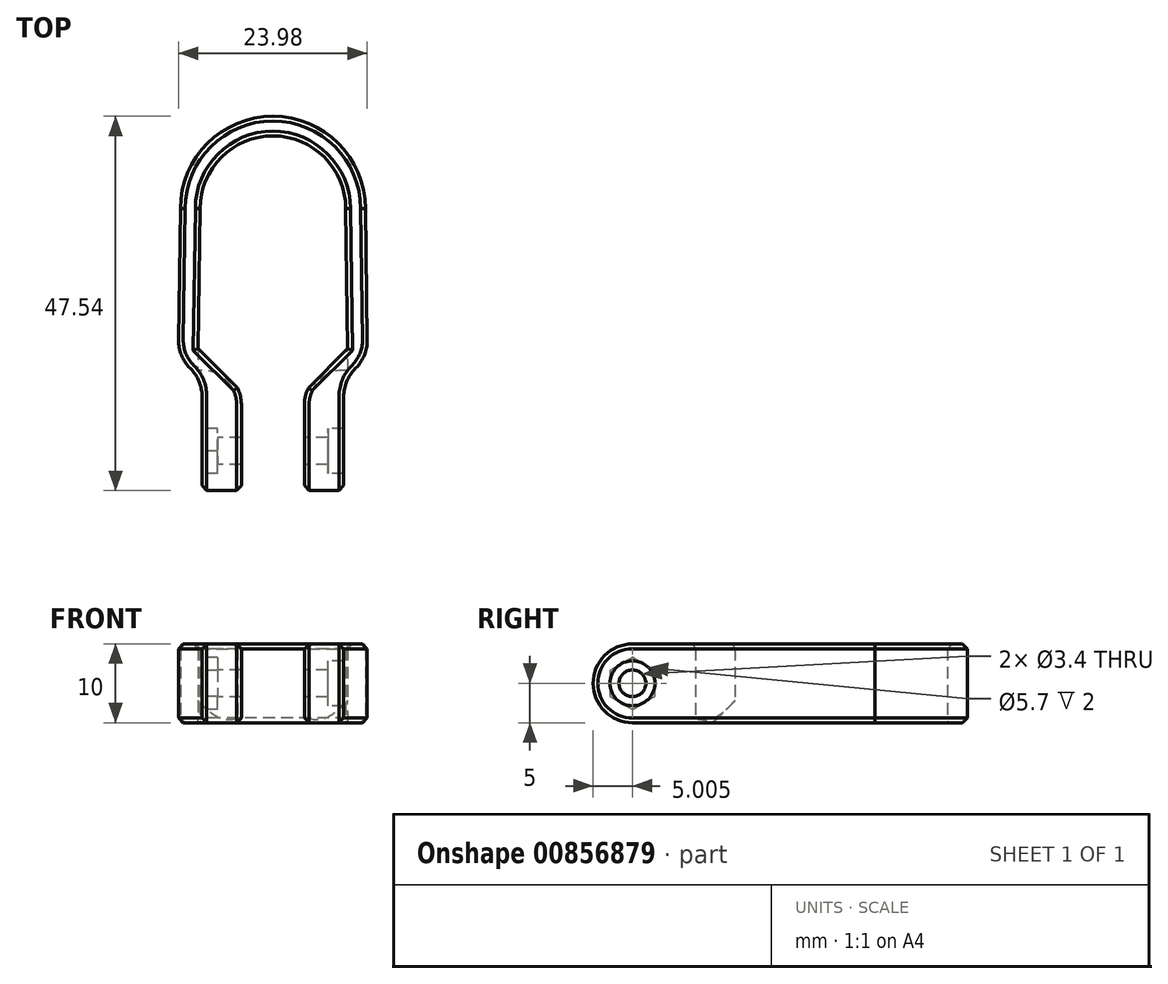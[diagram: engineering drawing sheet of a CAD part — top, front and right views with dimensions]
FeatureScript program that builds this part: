
annotation { "Feature Type Name" : "Feature", "Feature Type Description" : "" }
export const myFeature = defineFeature(function(context is Context, id is Id, definition is map)
    precondition{}
    {
        {
            var Q0;
            Q0=qCreatedBy(makeId("Top.planeOp"),FACE);
            var sketch = newSketch(context, id + "F0", { "sketchPlane" : qUnion([Q0])});
            skArc(sketch, "E0", {"start": v(9.25, 0) * mm, "mid": v(0, 9.25) * mm, "end": v(-9.25, 0) * mm});
            skLineSegment(sketch, "E1", {"start": v(-4.5, -22.75) * mm, "end": v(4.5, -22.75) * mm});
            skPoint(sketch, "E2", {"position": v(0, -22.75) * mm});
            skLineSegment(sketch, "E3", {"start": v(-9.5, -17.75) * mm, "end": v(-9.25, 0) * mm});
            skLineSegment(sketch, "E4", {"start": v(9.25, 0) * mm, "end": v(9.5, -17.75) * mm});
            skLineSegment(sketch, "E5", {"start": v(-9.5, -17.75) * mm, "end": v(-4.5, -22.75) * mm});
            skLineSegment(sketch, "E6.MirrorCS", {"start": v(9.5, -17.75) * mm, "end": v(4.5, -22.75) * mm});
            skPoint(sketch, "E7.orphan", {"position": v(-9.57, -22.75) * mm});
            skPoint(sketch, "E8.orphan", {"position": v(9.57, -22.75) * mm});
            skLineSegment(sketch, "E9.0", {"start": v(11.75, 0.02) * mm, "end": v(12.01, -18.77) * mm});
            skLineSegment(sketch, "E9.1", {"start": v(-4, -25.25) * mm, "end": v(5.54, -25.25) * mm});
            skLineSegment(sketch, "E9.2", {"start": v(-12.01, -18.77) * mm, "end": v(-5.54, -25.25) * mm});
            skLineSegment(sketch, "E9.3", {"start": v(12.01, -18.77) * mm, "end": v(5.54, -25.25) * mm});
            skLineSegment(sketch, "E9.4", {"start": v(-12.01, -18.77) * mm, "end": v(-11.75, 0.02) * mm});
            skArc(sketch, "E9.5", {"start": v(11.75, 0.02) * mm, "mid": v(0, 11.75) * mm, "end": v(-11.75, 0.02) * mm});
            skLineSegment(sketch, "E10", {"start": v(-4, -22.75) * mm, "end": v(-4, -25.25) * mm});
            skLineSegment(sketch, "E11.MirrorCS", {"start": v(4, -22.75) * mm, "end": v(4, -25.25) * mm});
            skLineSegment(sketch, "E12.bottom", {"start": v(-5.54, -25.25) * mm, "end": v(-3, -25.25) * mm});
            skLineSegment(sketch, "E13.bottom", {"start": v(-9, -21.79) * mm, "end": v(-4, -21.79) * mm});
            skLineSegment(sketch, "E13.top", {"start": v(-9, -35.79) * mm, "end": v(-4, -35.79) * mm});
            skLineSegment(sketch, "E13.left", {"start": v(-9, -21.79) * mm, "end": v(-9, -35.79) * mm});
            skLineSegment(sketch, "E13.right", {"start": v(-4, -21.79) * mm, "end": v(-4, -35.79) * mm});
            skLineSegment(sketch, "E14.MirrorCS", {"start": v(4, -21.79) * mm, "end": v(4, -35.79) * mm});
            skLineSegment(sketch, "E15.MirrorCS", {"start": v(9, -35.79) * mm, "end": v(4, -35.79) * mm});
            skLineSegment(sketch, "E16.MirrorCS", {"start": v(9, -21.79) * mm, "end": v(9, -35.79) * mm});
            skLineSegment(sketch, "E17.MirrorCS", {"start": v(9, -21.79) * mm, "end": v(4, -21.79) * mm});
            skSolve(sketch);
        }
        {
            var Q0;
            Q0=makeQuery(id+"F0.imprint","IMPRINT",FACE,{"disambiguationData":[TD([[makeQuery(id+"F0.imprint","IMPRINT",EDGE,{"derivedFrom":sQuery(id+"F0.wireOp",EDGE,"E0")}),-1.0]])]});
            var Q1;
            Q1=makeQuery(id+"F0.imprint","IMPRINT",FACE,{"disambiguationData":[TD([[makeQuery(id+"F0.imprint","IMPRINT",EDGE,{"derivedFrom":sQuery(id+"F0.wireOp",EDGE,"E12.bottom")}),-1.0]])]});
            var Q2;
            {var subQ0=sQuery(id+"F0.wireOp",EDGE,"b47a069d-5063-4df7-93ab-cb99865989350.MirrorCS");Q2=makeQuery(id+"F0.imprint","IMPRINT",FACE,{"disambiguationData":[TD([[makeQuery(id+"F0.imprint","IMPRINT",EDGE,{"derivedFrom":subQ0}),-1.0]])]});}
            var Q3;
            {var subQ0=sQuery(id+"F0.wireOp",EDGE,"E15.MirrorCS");Q3=makeQuery(id+"F0.imprint","IMPRINT",FACE,{"disambiguationData":[TD([[makeQuery(id+"F0.imprint","IMPRINT",EDGE,{"derivedFrom":subQ0}),-1.0]])]});}
            var Q4;
            {var subQ7=sQuery(id+"F0.wireOp",EDGE,"E5");var subQ8=sQuery(id+"F0.wireOp",EDGE,"E1");var subQ9=makeQuery(id+"F0.imprint","INTERSECT",VERTEX,{"derivedFrom":[subQ8,subQ7]});Q4=makeQuery(id+"F0.imprint","IMPRINT",FACE,{"disambiguationData":[TD([[makeQuery(id+"F0.imprint","IMPRINT",EDGE,{"disambiguationData":[TD([[subQ9,-1.0]])],"derivedFrom":subQ8}),-1.0]])]});}
            var Q5;
            {var subQ7=sQuery(id+"F0.wireOp",EDGE,"E6.MirrorCS");var subQ8=sQuery(id+"F0.wireOp",EDGE,"E1");var subQ9=makeQuery(id+"F0.imprint","INTERSECT",VERTEX,{"derivedFrom":[subQ8,subQ7]});Q5=makeQuery(id+"F0.imprint","IMPRINT",FACE,{"disambiguationData":[TD([[makeQuery(id+"F0.imprint","IMPRINT",EDGE,{"disambiguationData":[TD([[subQ9,1.0]])],"derivedFrom":subQ8}),-1.0]])]});}
            extrude(context, id + "F1", {"entities" : qUnion([Q0, Q1, Q2, Q3, Q4, Q5]), "depth" : 10 * mm, "offsetDistance" : 25 * mm});
        }
        {
            var Q0;
            Q0=makeQuery(id+"F1.opExtrude","CAP_EDGE",EDGE,{"disambiguationData":[OSD([sQuery(id+"F0.wireOp",EDGE,"E12.top")])],"isStart":false});
            var Q1;
            Q1=makeQuery(id+"F1.opExtrude","CAP_EDGE",EDGE,{"disambiguationData":[OSD([sQuery(id+"F0.wireOp",EDGE,"62c8df0b-8da3-4cad-a578-fa849236712b0.MirrorCS")])],"isStart":false});
            var Q2;
            Q2=makeQuery(id+"F1.opExtrude","CAP_EDGE",EDGE,{"disambiguationData":[OSD([sQuery(id+"F0.wireOp",EDGE,"62c8df0b-8da3-4cad-a578-fa849236712b0.MirrorCS")])],"isStart":true});
            var Q3;
            Q3=makeQuery(id+"F1.opExtrude","CAP_EDGE",EDGE,{"disambiguationData":[OSD([sQuery(id+"F0.wireOp",EDGE,"E12.top")])],"isStart":true});
            var Q4;
            Q4=makeQuery(id+"F1.opExtrude","CAP_EDGE",EDGE,{"disambiguationData":[OSD([sQuery(id+"F0.wireOp",EDGE,"E13.top")])],"isStart":false});
            var Q5;
            Q5=makeQuery(id+"F1.opExtrude","CAP_EDGE",EDGE,{"disambiguationData":[OSD([sQuery(id+"F0.wireOp",EDGE,"E13.top")])],"isStart":true});
            var Q6;
            Q6=makeQuery(id+"F1.opExtrude","CAP_EDGE",EDGE,{"disambiguationData":[OSD([sQuery(id+"F0.wireOp",EDGE,"E15.MirrorCS")])],"isStart":false});
            var Q7;
            Q7=makeQuery(id+"F1.opExtrude","CAP_EDGE",EDGE,{"disambiguationData":[OSD([sQuery(id+"F0.wireOp",EDGE,"E15.MirrorCS")])],"isStart":true});
            fillet(context, id + "F2", {"entities" : qUnion([Q0, Q1, Q2, Q3, Q4, Q5, Q6, Q7]), "radius" : 5 * mm, "tangentPropagation" : true, "allowEdgeOverflow" : false});
        }
        {
            var Q0;
            Q0=makeQuery(id+"F1.opExtrude","SWEPT_FACE",FACE,{"disambiguationData":[OSD([sQuery(id+"F0.wireOp",EDGE,"E13.left")])]});
            var sketch = newSketch(context, id + "F3", { "sketchPlane" : qUnion([Q0])});
            skCircle(sketch, "E18", {"center": v(30.79, 5) * mm, "radius": 1.7 * mm});
            skPoint(sketch, "E18.centerSnap0", {"position": v(35.79, 5) * mm});
            skCircle(sketch, "E19.cCircle", {"center": v(30.79, 5) * mm, "radius": 2.85 * mm});
            skLineSegment(sketch, "E19.0", {"start": v(27.94, 3.35) * mm, "end": v(27.94, 6.65) * mm});
            skLineSegment(sketch, "E19.1", {"start": v(27.94, 6.65) * mm, "end": v(30.79, 8.3) * mm});
            skLineSegment(sketch, "E19.2", {"start": v(30.79, 8.3) * mm, "end": v(33.64, 6.65) * mm});
            skLineSegment(sketch, "E19.3", {"start": v(33.64, 6.65) * mm, "end": v(33.64, 3.35) * mm});
            skLineSegment(sketch, "E19.4", {"start": v(33.64, 3.35) * mm, "end": v(30.79, 1.7) * mm});
            skLineSegment(sketch, "E19.5", {"start": v(30.79, 1.7) * mm, "end": v(27.94, 3.35) * mm});
            skPoint(sketch, "E19.0.midPoint", {"position": v(27.94, 5) * mm});
            skSolve(sketch);
        }
        {
            var Q0;
            Q0=makeQuery(id+"F3.imprint","IMPRINT",FACE,{"disambiguationData":[TD([[makeQuery(id+"F3.imprint","IMPRINT",EDGE,{"derivedFrom":sQuery(id+"F3.wireOp",EDGE,"E18")}),1.0]])]});
            extrude(context, id + "F4", {"entities" : qUnion([Q0]), "operationType" : NewBodyOperationType.REMOVE, "endBound" : BoundingType.THROUGH_ALL, "oppositeDirection" : true, "depth" : 25 * mm, "offsetDistance" : 25 * mm});
        }
        {
            var Q0;
            Q0=makeQuery(id+"F3.imprint","IMPRINT",FACE,{"disambiguationData":[TD([[makeQuery(id+"F3.imprint","IMPRINT",EDGE,{"derivedFrom":sQuery(id+"F3.wireOp",EDGE,"E18")}),-1.0]])]});
            var Q1;
            {var subQ0=sQuery(id+"F3.wireOp",EDGE,"E19.0");var subQ1=sQuery(id+"F3.wireOp",EDGE,"E19.cCircle");var subQ2=makeQuery(id+"F3.imprint","INTERSECT",VERTEX,{"derivedFrom":[subQ1,subQ0]});Q1=makeQuery(id+"F3.imprint","IMPRINT",FACE,{"disambiguationData":[TD([[makeQuery(id+"F3.imprint","IMPRINT",EDGE,{"disambiguationData":[TD([[subQ2,-1.0]])],"derivedFrom":subQ1}),-1.0]])]});}
            var Q2;
            {var subQ0=sQuery(id+"F3.wireOp",EDGE,"E19.1");var subQ1=sQuery(id+"F3.wireOp",EDGE,"E19.cCircle");var subQ2=makeQuery(id+"F3.imprint","INTERSECT",VERTEX,{"derivedFrom":[subQ1,subQ0]});Q2=makeQuery(id+"F3.imprint","IMPRINT",FACE,{"disambiguationData":[TD([[makeQuery(id+"F3.imprint","IMPRINT",EDGE,{"disambiguationData":[TD([[subQ2,-1.0]])],"derivedFrom":subQ1}),-1.0]])]});}
            var Q3;
            {var subQ0=sQuery(id+"F3.wireOp",EDGE,"E19.2");var subQ1=sQuery(id+"F3.wireOp",EDGE,"E19.cCircle");var subQ2=makeQuery(id+"F3.imprint","INTERSECT",VERTEX,{"derivedFrom":[subQ1,subQ0]});Q3=makeQuery(id+"F3.imprint","IMPRINT",FACE,{"disambiguationData":[TD([[makeQuery(id+"F3.imprint","IMPRINT",EDGE,{"disambiguationData":[TD([[subQ2,-1.0]])],"derivedFrom":subQ1}),-1.0]])]});}
            var Q4;
            {var subQ0=sQuery(id+"F3.wireOp",EDGE,"E19.2");var subQ1=sQuery(id+"F3.wireOp",EDGE,"E19.cCircle");var subQ2=makeQuery(id+"F3.imprint","INTERSECT",VERTEX,{"derivedFrom":[subQ1,subQ0]});Q4=makeQuery(id+"F3.imprint","IMPRINT",FACE,{"disambiguationData":[TD([[makeQuery(id+"F3.imprint","IMPRINT",EDGE,{"disambiguationData":[TD([[subQ2,1.0]])],"derivedFrom":subQ1}),-1.0]])]});}
            var Q5;
            {var subQ0=sQuery(id+"F3.wireOp",EDGE,"E19.3");var subQ1=sQuery(id+"F3.wireOp",EDGE,"E19.cCircle");var subQ2=makeQuery(id+"F3.imprint","INTERSECT",VERTEX,{"derivedFrom":[subQ1,subQ0]});Q5=makeQuery(id+"F3.imprint","IMPRINT",FACE,{"disambiguationData":[TD([[makeQuery(id+"F3.imprint","IMPRINT",EDGE,{"disambiguationData":[TD([[subQ2,1.0]])],"derivedFrom":subQ1}),-1.0]])]});}
            var Q6;
            {var subQ0=sQuery(id+"F3.wireOp",EDGE,"E19.5");var subQ1=sQuery(id+"F3.wireOp",EDGE,"E19.cCircle");var subQ2=makeQuery(id+"F3.imprint","INTERSECT",VERTEX,{"derivedFrom":[subQ1,subQ0]});Q6=makeQuery(id+"F3.imprint","IMPRINT",FACE,{"disambiguationData":[TD([[makeQuery(id+"F3.imprint","IMPRINT",EDGE,{"disambiguationData":[TD([[subQ2,-1.0]])],"derivedFrom":subQ1}),-1.0]])]});}
            extrude(context, id + "F5", {"entities" : qUnion([Q0, Q1, Q2, Q3, Q4, Q5, Q6]), "operationType" : NewBodyOperationType.REMOVE, "oppositeDirection" : true, "depth" : 2 * mm, "offsetDistance" : 25 * mm});
        }
        {
            var Q0;
            Q0=makeQuery(id+"F3.imprint","IMPRINT",FACE,{"disambiguationData":[TD([[makeQuery(id+"F3.imprint","IMPRINT",EDGE,{"derivedFrom":sQuery(id+"F3.wireOp",EDGE,"E18")}),-1.0]])]});
            var Q1;
            Q1=makeQuery(id+"F1.opExtrude","SWEPT_FACE",FACE,{"disambiguationData":[OSD([sQuery(id+"F0.wireOp",EDGE,"E16.MirrorCS")])]});
            var Q2;
            Q2=makeQuery(id+"F1.opExtrude","SWEPT_FACE",FACE,{"disambiguationData":[OSD([sQuery(id+"F0.wireOp",EDGE,"E14.MirrorCS")])]});
            extrude(context, id + "F6", {"entities" : qUnion([Q0]), "operationType" : NewBodyOperationType.REMOVE, "endBound" : BoundingType.UP_TO_SURFACE, "oppositeDirection" : true, "depth" : 25 * mm, "endBoundEntityFace" : qUnion([Q1]), "offsetDistance" : 25 * mm, "hasSecondDirection" : true, "secondDirectionBound" : SecondDirectionBoundingType.UP_TO_SURFACE, "secondDirectionOppositeDirection" : true, "secondDirectionDepth" : 9.7 * mm, "secondDirectionBoundEntityFace" : qUnion([Q2]), "hasSecondDirectionOffset" : true, "secondDirectionOffsetDistance" : -3 * mm});
        }
        {
            var Q0;
            Q0=makeQuery(id+"F1.opExtrude","SWEPT_EDGE",EDGE,{"disambiguationData":[OSD([sQuery(id+"F0.wireOp",EDGE,"E9.2"),sQuery(id+"F0.wireOp",EDGE,"E13.bottom"),sQuery(id+"F0.wireOp",EDGE,"E13.left")])]});
            var Q1;
            Q1=makeQuery(id+"F1.opExtrude","SWEPT_EDGE",EDGE,{"disambiguationData":[OSD([sQuery(id+"F0.wireOp",EDGE,"E9.3"),sQuery(id+"F0.wireOp",EDGE,"E16.MirrorCS"),sQuery(id+"F0.wireOp",EDGE,"E17.MirrorCS")])]});
            var Q2;
            Q2=makeQuery(id+"F1.opExtrude","SWEPT_EDGE",EDGE,{"disambiguationData":[OSD([sQuery(id+"F0.wireOp",EDGE,"E9.0"),sQuery(id+"F0.wireOp",EDGE,"E9.3")])]});
            var Q3;
            Q3=makeQuery(id+"F1.opExtrude","SWEPT_EDGE",EDGE,{"disambiguationData":[OSD([sQuery(id+"F0.wireOp",EDGE,"E9.2"),sQuery(id+"F0.wireOp",EDGE,"E9.4")])]});
            fillet(context, id + "F7", {"entities" : qUnion([Q0, Q1, Q2, Q3]), "radius" : 5 * mm, "tangentPropagation" : true, "allowEdgeOverflow" : false});
        }
        {
            var Q0;
            Q0=makeQuery(id+"F1.opExtrude","SWEPT_EDGE",EDGE,{"disambiguationData":[OSD([sQuery(id+"F0.wireOp",EDGE,"E1"),sQuery(id+"F0.wireOp",EDGE,"E13.right")])]});
            var Q1;
            Q1=makeQuery(id+"F1.opExtrude","SWEPT_EDGE",EDGE,{"disambiguationData":[OSD([sQuery(id+"F0.wireOp",EDGE,"E1"),sQuery(id+"F0.wireOp",EDGE,"E14.MirrorCS")])]});
            fillet(context, id + "F8", {"entities" : qUnion([Q0, Q1]), "radius" : 5 * mm, "tangentPropagation" : true, "allowEdgeOverflow" : false});
        }
        {
            var Q0;
            Q0=makeQuery(id+"F1.opExtrude","CAP_FACE",FACE,{"disambiguationData":[OSD([sQuery(id+"F0.wireOp",EDGE,"E0"),sQuery(id+"F0.wireOp",EDGE,"E1"),sQuery(id+"F0.wireOp",EDGE,"E3"),sQuery(id+"F0.wireOp",EDGE,"E4"),sQuery(id+"F0.wireOp",EDGE,"E5"),sQuery(id+"F0.wireOp",EDGE,"E6.MirrorCS"),sQuery(id+"F0.wireOp",EDGE,"E9.0"),sQuery(id+"F0.wireOp",EDGE,"E9.2"),sQuery(id+"F0.wireOp",EDGE,"E9.3"),sQuery(id+"F0.wireOp",EDGE,"E9.4"),sQuery(id+"F0.wireOp",EDGE,"E9.5"),sQuery(id+"F0.wireOp",EDGE,"E13.top"),sQuery(id+"F0.wireOp",EDGE,"E13.left"),sQuery(id+"F0.wireOp",EDGE,"E13.right"),sQuery(id+"F0.wireOp",EDGE,"E14.MirrorCS"),sQuery(id+"F0.wireOp",EDGE,"E15.MirrorCS"),sQuery(id+"F0.wireOp",EDGE,"E16.MirrorCS")])],"isStart":false});
            chamfer(context, id + "F9", {"entities" : qUnion([Q0]), "width" : .6 * mm, "tangentPropagation" : true});
        }
        {
            var Q0;
            Q0=makeQuery(id+"F1.opExtrude","CAP_EDGE",EDGE,{"disambiguationData":[OSD([sQuery(id+"F0.wireOp",EDGE,"E9.5")])],"isStart":true});
            chamfer(context, id + "F10", {"entities" : qUnion([Q0]), "width" : .6 * mm, "tangentPropagation" : true});
        }
    });
